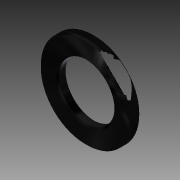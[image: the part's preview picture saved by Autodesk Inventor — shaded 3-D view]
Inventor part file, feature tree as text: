
AUTODESK INVENTOR PART (.ipt)
format: ipt  version: 2014 (Build 180170000, 170)  size: 91,136 bytes
history: native  units: mm (DEFAULTED — no unit token found)
features: sketch x2, plane x1, extrude x1, chamfer x1, reference x1
ambient origin geometry x8: Origin, YZ Plane, XZ Plane, XY Plane, X Axis, Y Axis, Z Axis, Center Point
bodies: Solid1 (feature_tree)
feature tree (6):
  sketch  "Sketch1"  dims[d2=0.79375mm d3=0.0mm d4=0.127mm d5=0.127mm]
  plane  "Work Plane1"
  extrude  "Extrusion1"  Depth=0.79375mm
  chamfer  "Chamfer1"  [1 undecoded]
  sketch  "Sketch2"  dims[d6=45.0deg]
  reference  "Reference1"
note: 1 required parameter value undecoded (feature->parameter linkage not recoverable at this tier; creation-order binding heuristic only, values carry confidence <= 0.55)
